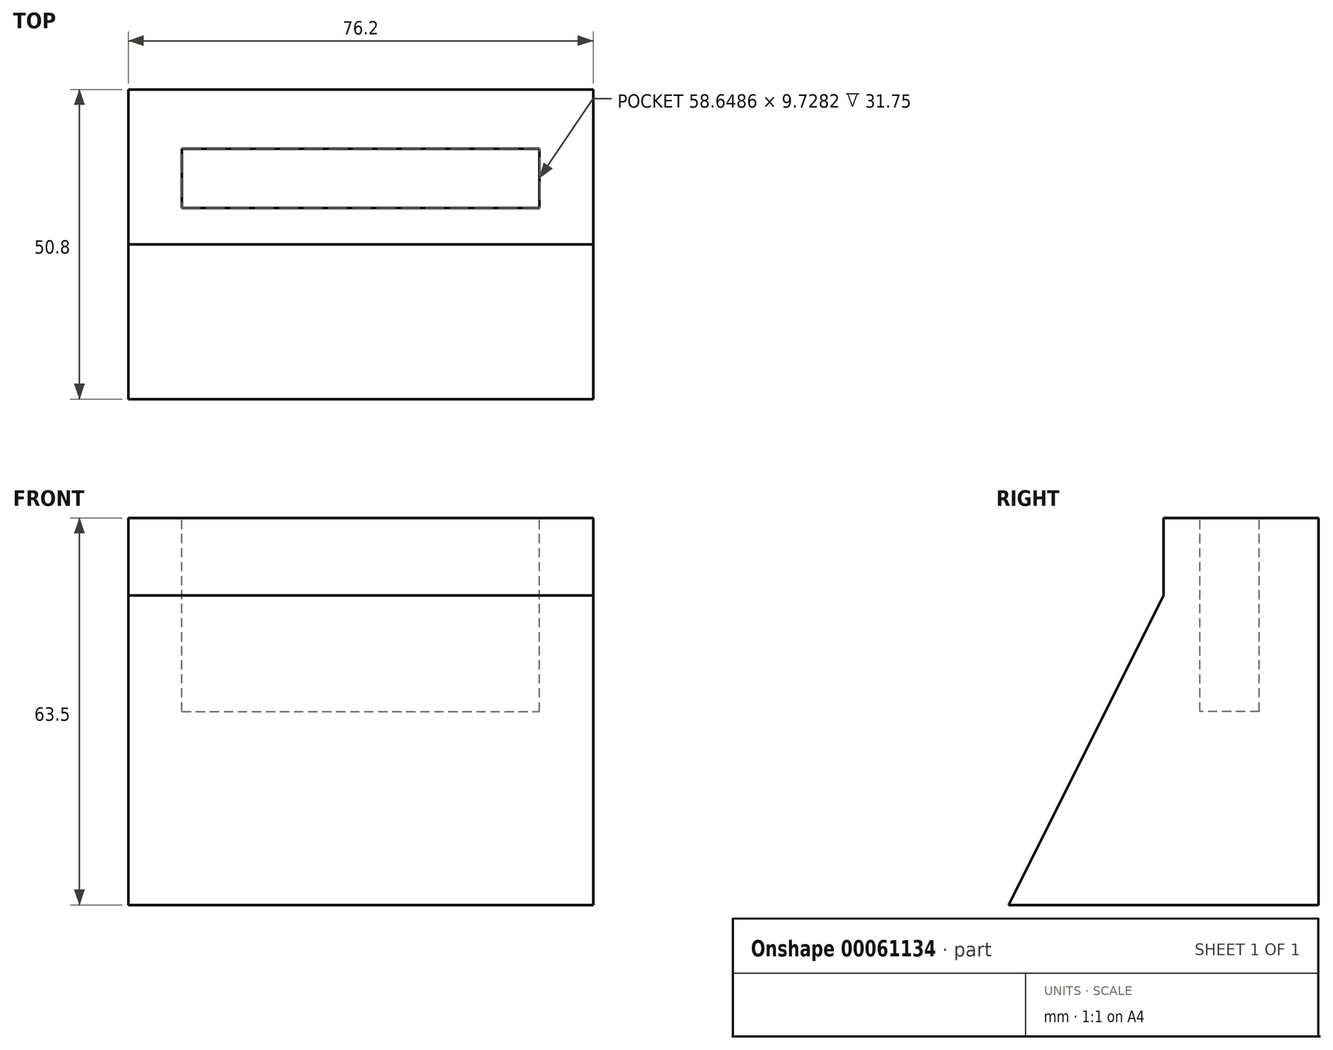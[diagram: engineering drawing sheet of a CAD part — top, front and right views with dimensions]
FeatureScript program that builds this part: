
annotation { "Feature Type Name" : "Feature", "Feature Type Description" : "" }
export const myFeature = defineFeature(function(context is Context, id is Id, definition is map)
    precondition{}
    {
        {
            var Q0;
            Q0=qCreatedBy(makeId("Top.planeOp"),FACE);
            var sketch = newSketch(context, id + "F0", { "sketchPlane" : qUnion([Q0])});
            skLineSegment(sketch, "E0.bottom", {"start": v(-31.1, 20.4) * mm, "end": v(45.1, 20.4) * mm});
            skLineSegment(sketch, "E0.top", {"start": v(-31.1, -30.4) * mm, "end": v(45.1, -30.4) * mm});
            skLineSegment(sketch, "E0.left", {"start": v(-31.1, 20.4) * mm, "end": v(-31.1, -30.4) * mm});
            skLineSegment(sketch, "E0.right", {"start": v(45.1, 20.4) * mm, "end": v(45.1, -30.4) * mm});
            skSolve(sketch);
        }
        {
            var Q0;
            Q0 = qSketchRegion(id + "F0", true);
            extrude(context, id + "F1", {"entities" : qUnion([Q0]), "depth" : 50.8 * mm});
        }
        {
            var Q0;
            Q0=makeQuery(id+"F1.opExtrude","CAP_FACE",FACE,{"disambiguationData":[OSD([sQuery(id+"F0.wireOp",EDGE,"E0.bottom"),sQuery(id+"F0.wireOp",EDGE,"E0.top"),sQuery(id+"F0.wireOp",EDGE,"E0.left"),sQuery(id+"F0.wireOp",EDGE,"E0.right")])],"isStart":false});
            var sketch = newSketch(context, id + "F2", { "sketchPlane" : qUnion([Q0])});
            skPoint(sketch, "E1", {"position": v(-22.32, 20.4) * mm});
            skPoint(sketch, "E2", {"position": v(36.33, 20.4) * mm});
            skPoint(sketch, "E3", {"position": v(-22.32, 10.67) * mm});
            skPoint(sketch, "E4", {"position": v(-22.32, 0.94) * mm});
            skLineSegment(sketch, "E5", {"start": v(-22.32, 10.67) * mm, "end": v(36.33, 10.67) * mm});
            skLineSegment(sketch, "E6", {"start": v(36.33, 10.67) * mm, "end": v(36.33, 0.94) * mm});
            skLineSegment(sketch, "E7", {"start": v(36.33, 0.94) * mm, "end": v(-22.32, 0.94) * mm});
            skLineSegment(sketch, "E8", {"start": v(-22.32, 10.67) * mm, "end": v(-22.32, 0.94) * mm});
            skSolve(sketch);
        }
        {
            var Q0;
            Q0 = qSketchRegion(id + "F2", true);
            extrude(context, id + "F3", {"entities" : qUnion([Q0]), "operationType" : NewBodyOperationType.REMOVE, "oppositeDirection" : true, "depth" : 19.05 * mm});
        }
        {
            var Q0;
            Q0=makeQuery(id+"F1.opExtrude","SWEPT_FACE",FACE,{"disambiguationData":[OSD([sQuery(id+"F0.wireOp",EDGE,"E0.left")])]});
            var sketch = newSketch(context, id + "F4", { "sketchPlane" : qUnion([Q0])});
            skPoint(sketch, "E9", {"position": v(5, 50.8) * mm});
            skLineSegment(sketch, "E10", {"start": v(5, 50.8) * mm, "end": v(30.4, 0) * mm});
            skSolve(sketch);
        }
        {
            var Q0;
            Q0 = qSketchRegion(id + "F4", true);
            var Q1;
            {var subQ0=sQuery(id+"F4.wireOp",EDGE,"E10");Q1=makeQuery(id+"F4.imprint","IMPRINT",FACE,{"disambiguationData":[TD([[makeQuery(id+"F4.imprint","IMPRINT",EDGE,{"derivedFrom":subQ0}),1.0]])]});}
            extrude(context, id + "F5", {"entities" : qUnion([Q0, Q1]), "operationType" : NewBodyOperationType.REMOVE, "oppositeDirection" : true, "depth" : 76.2 * mm});
        }
        {
            var Q0;
            Q0=makeQuery(id+"F1.opExtrude","CAP_FACE",FACE,{"disambiguationData":[OSD([sQuery(id+"F0.wireOp",EDGE,"E0.bottom"),sQuery(id+"F0.wireOp",EDGE,"E0.top"),sQuery(id+"F0.wireOp",EDGE,"E0.left"),sQuery(id+"F0.wireOp",EDGE,"E0.right")])],"isStart":false});
            extrude(context, id + "F6", {"entities" : qUnion([Q0]), "operationType" : NewBodyOperationType.ADD, "depth" : 12.7 * mm});
        }
    });
